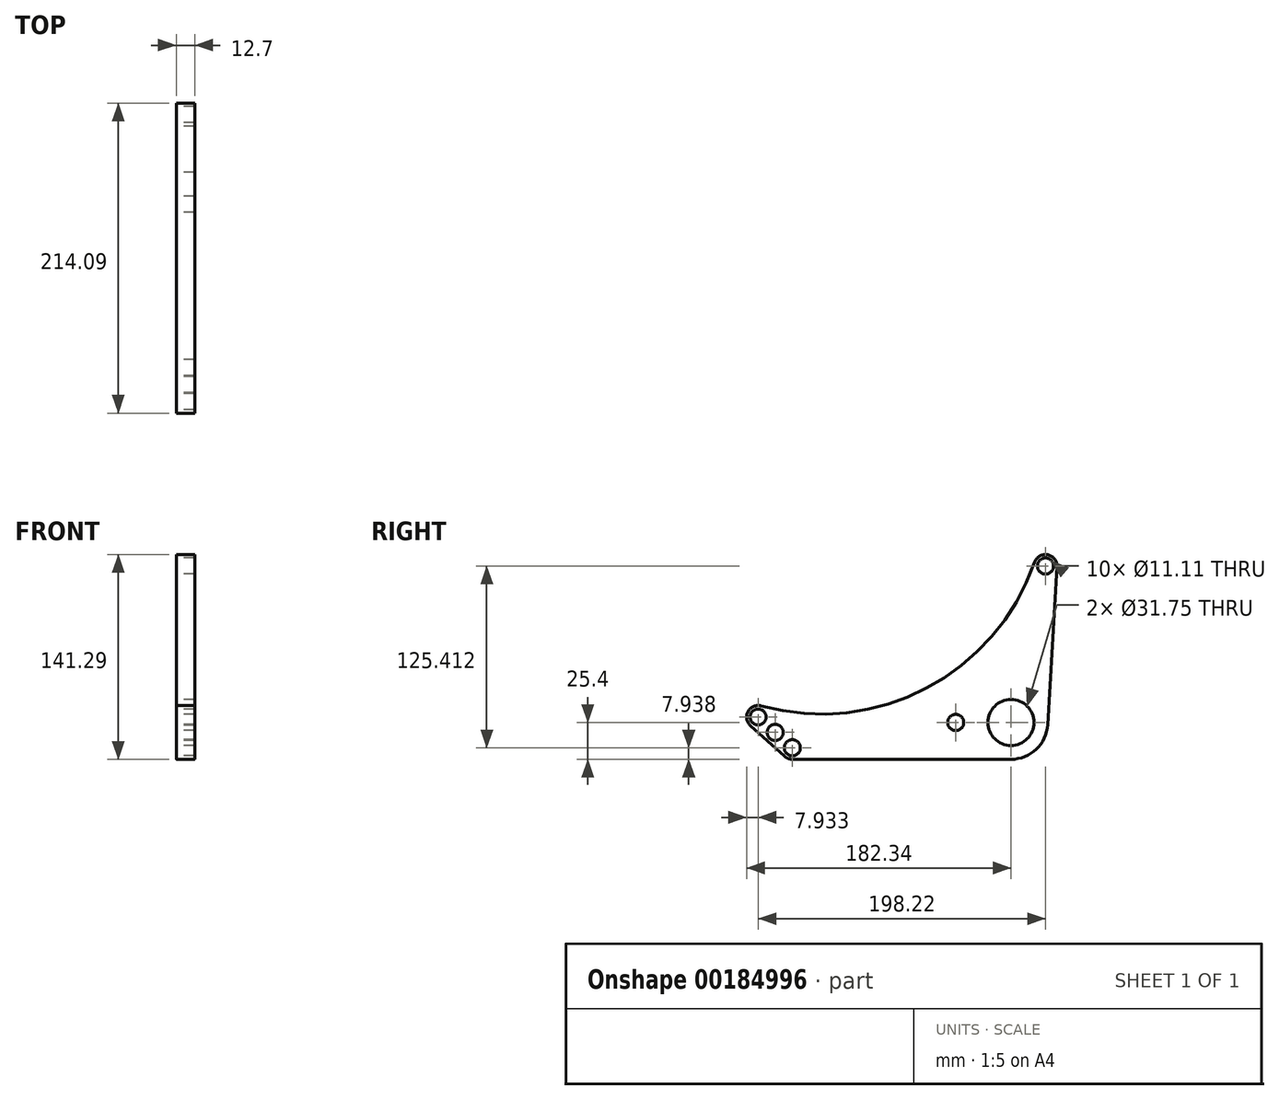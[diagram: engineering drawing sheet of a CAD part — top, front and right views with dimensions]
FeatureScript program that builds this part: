
annotation { "Feature Type Name" : "Feature", "Feature Type Description" : "" }
export const myFeature = defineFeature(function(context is Context, id is Id, definition is map)
    precondition{}
    {
        {
            var Q0;
            Q0=qCreatedBy(makeId("Right.planeOp"),FACE);
            var sketch = newSketch(context, id + "F0", { "sketchPlane" : qUnion([Q0])});
            skCircle(sketch, "E0", {"center": v(0, 0) * mm, "radius": 15.88 * mm});
            skArc(sketch, "E1", {"start": v(0, -25.4) * mm, "mid": v(17.43, -18.48) * mm, "end": v(25.36, -1.48) * mm});
            skLineSegment(sketch, "E2", {"start": v(0, -25.4) * mm, "end": v(-150.81, -25.4) * mm});
            skArc(sketch, "E3", {"start": v(-156.12, -23.36) * mm, "mid": v(-153.66, -24.87) * mm, "end": v(-150.81, -25.4) * mm});
            skCircle(sketch, "E4", {"center": v(-150.81, -17.46) * mm, "radius": 5.56 * mm});
            skLineSegment(sketch, "E5", {"start": v(-150.81, -17.46) * mm, "end": v(-174.4, 3.78) * mm, "construction": true});
            skCircle(sketch, "E6", {"center": v(-174.4, 3.78) * mm, "radius": 5.56 * mm});
            skCircle(sketch, "E7", {"center": v(-162.6, -6.84) * mm, "radius": 5.56 * mm});
            skArc(sketch, "E8", {"start": v(-172.29, 11.43) * mm, "mid": v(-181.37, 7.6) * mm, "end": v(-179.72, -2.12) * mm});
            skLineSegment(sketch, "E9", {"start": v(-179.72, -2.12) * mm, "end": v(-156.12, -23.36) * mm});
            skCircle(sketch, "E10", {"center": v(23.81, 107.95) * mm, "radius": 5.56 * mm});
            skArc(sketch, "E11", {"start": v(31.74, 107.49) * mm, "mid": v(25.36, 115.74) * mm, "end": v(16.31, 110.54) * mm});
            skLineSegment(sketch, "E12", {"start": v(31.74, 107.49) * mm, "end": v(25.36, -1.48) * mm});
            skArc(sketch, "E13", {"start": v(-172.29, 11.43) * mm, "mid": v(-58.36, 23.64) * mm, "end": v(16.31, 110.54) * mm});
            skCircle(sketch, "E14", {"center": v(-38.1, 0) * mm, "radius": 5.56 * mm});
            skSolve(sketch);
        }
        {
            var Q0;
            Q0=makeQuery(id+"F0.imprint","IMPRINT",FACE,{"disambiguationData":[TD([[makeQuery(id+"F0.imprint","IMPRINT",EDGE,{"derivedFrom":sQuery(id+"F0.wireOp",EDGE,"E0")}),-1.0]])]});
            extrude(context, id + "F1", {"entities" : qUnion([Q0]), "depth" : 12.7 * mm, "offsetDistance" : 25.4 * mm});
        }
    });
